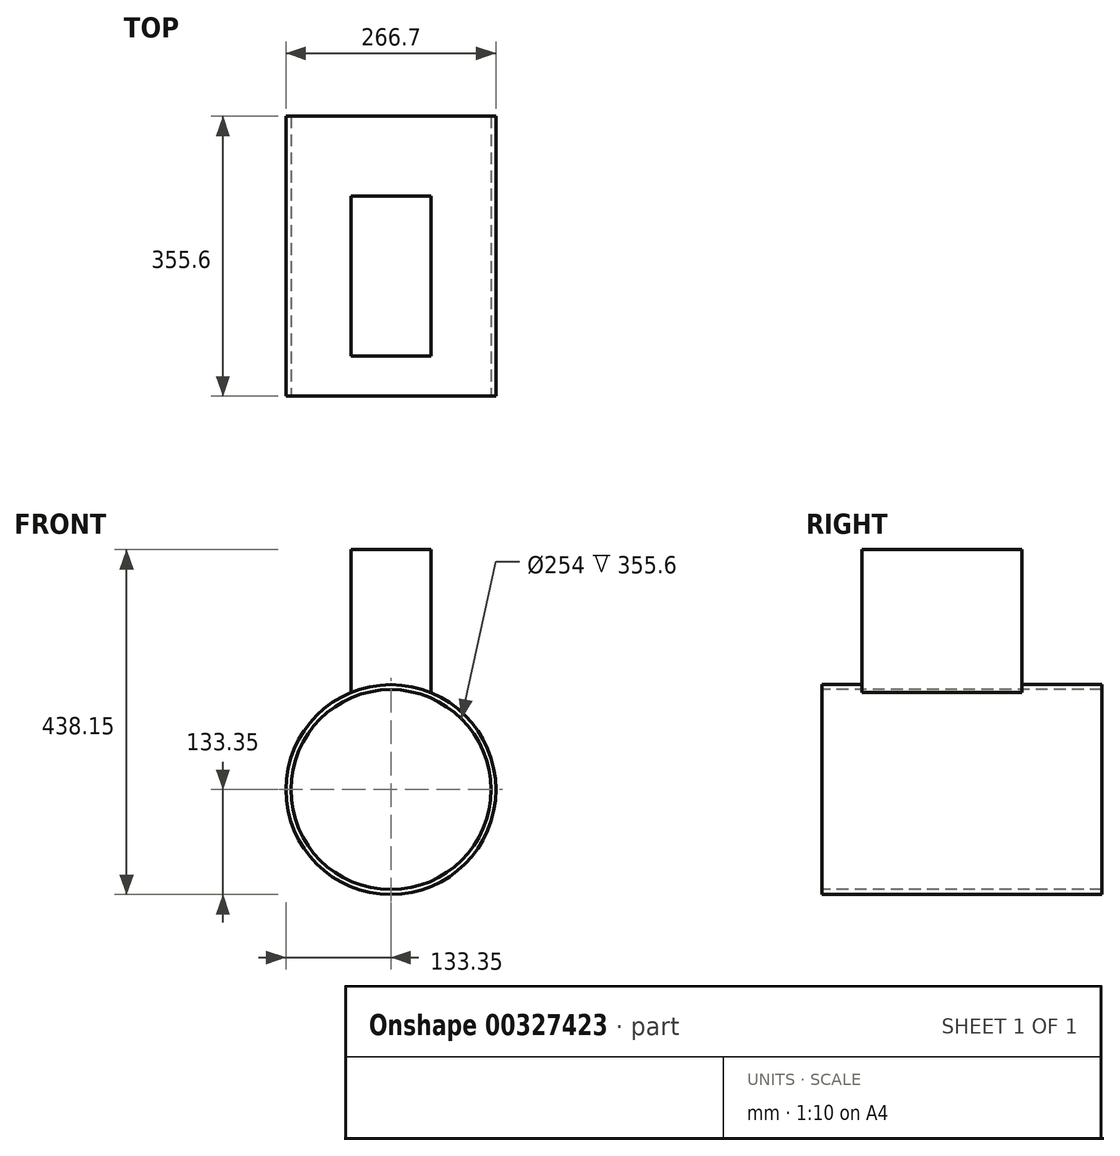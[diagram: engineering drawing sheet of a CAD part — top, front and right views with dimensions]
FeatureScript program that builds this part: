
annotation { "Feature Type Name" : "Feature", "Feature Type Description" : "" }
export const myFeature = defineFeature(function(context is Context, id is Id, definition is map)
    precondition{}
    {
        {
            var Q0;
            Q0=qCreatedBy(makeId("Front.planeOp"),FACE);
            var sketch = newSketch(context, id + "F0", { "sketchPlane" : qUnion([Q0])});
            skCircle(sketch, "E0", {"center": v(0, 0) * mm, "radius": 133.35 * mm});
            skSolve(sketch);
        }
        {
            var Q0;
            Q0=qSketchRegion(id+"F0",true);
            extrude(context, id + "F1", {"entities" : qUnion([Q0]), "depth" : 355.6 * mm});
        }
        {
            var Q0;
            Q0=qCreatedBy(makeId("Top.planeOp"),FACE);
            var sketch = newSketch(context, id + "F2", { "sketchPlane" : qUnion([Q0])});
            skLineSegment(sketch, "E1.bottom", {"start": v(-50.8, -101.6) * mm, "end": v(50.8, -101.6) * mm});
            skLineSegment(sketch, "E1.top", {"start": v(-50.8, -304.8) * mm, "end": v(50.8, -304.8) * mm});
            skLineSegment(sketch, "E1.left", {"start": v(-50.8, -101.6) * mm, "end": v(-50.8, -304.8) * mm});
            skLineSegment(sketch, "E1.right", {"start": v(50.8, -101.6) * mm, "end": v(50.8, -304.8) * mm});
            skPoint(sketch, "E2", {"position": v(0, -101.6) * mm});
            skSolve(sketch);
        }
        {
            var Q0;
            Q0=qSketchRegion(id+"F2",true);
            extrude(context, id + "F3", {"entities" : qUnion([Q0]), "operationType" : NewBodyOperationType.ADD, "depth" : 304.8 * mm});
        }
        {
            var Q0;
            Q0=makeQuery(id+"F1.opExtrude","CAP_FACE",FACE,{"disambiguationData":[OSD([sQuery(id+"F0.wireOp",EDGE,"E0")])],"isStart":false});
            var sketch = newSketch(context, id + "F4", { "sketchPlane" : qUnion([Q0])});
            skCircle(sketch, "E3", {"center": v(0, 0) * mm, "radius": 127 * mm});
            skSolve(sketch);
        }
        {
            var Q0;
            Q0=qSketchRegion(id+"F4",true);
            extrude(context, id + "F5", {"entities" : qUnion([Q0]), "operationType" : NewBodyOperationType.REMOVE, "endBound" : BoundingType.THROUGH_ALL, "oppositeDirection" : true, "depth" : 25.4 * mm});
        }
    });
